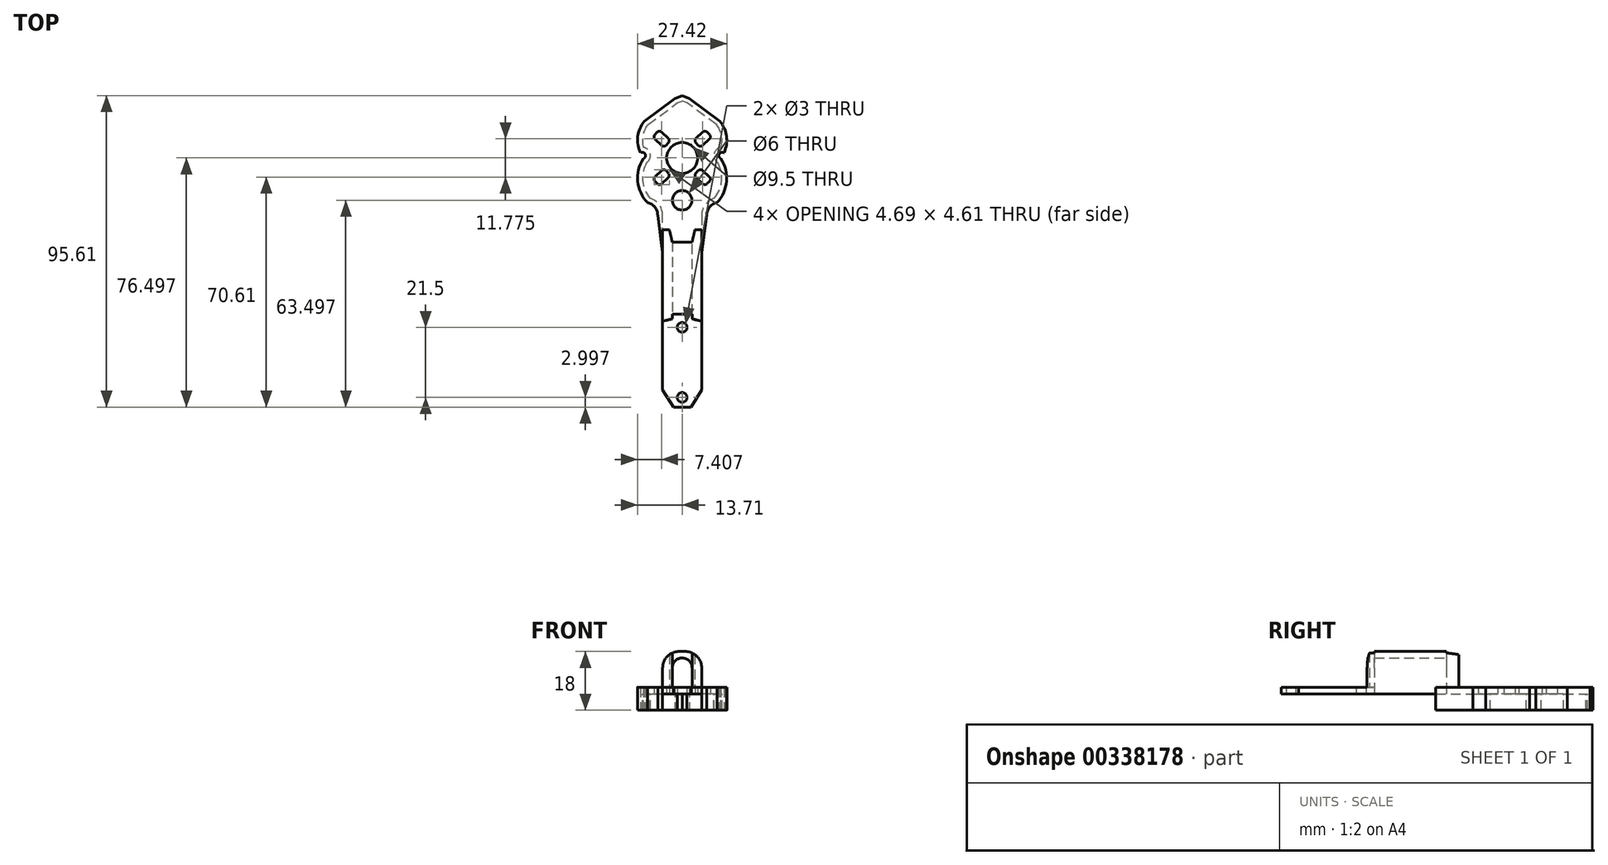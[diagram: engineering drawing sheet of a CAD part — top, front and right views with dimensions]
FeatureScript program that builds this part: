
annotation { "Feature Type Name" : "Feature", "Feature Type Description" : "" }
export const myFeature = defineFeature(function(context is Context, id is Id, definition is map)
    precondition{}
    {
        {
            var Q0;
            Q0=qCreatedBy(makeId("Top.planeOp"),FACE);
            var sketch = newSketch(context, id + "F0", { "sketchPlane" : qUnion([Q0])});
            skLineSegment(sketch, "E0", {"start": v(0, 46.56) * mm, "end": v(0, -47.44) * mm});
            skLineSegment(sketch, "E1", {"start": v(0, 0) * mm, "end": v(6, 0) * mm});
            skLineSegment(sketch, "E2", {"start": v(0, -47.44) * mm, "end": v(0, -44.44) * mm});
            skLineSegment(sketch, "E3", {"start": v(0, -47.44) * mm, "end": v(0, -24.44) * mm});
            skLineSegment(sketch, "E4", {"start": v(0, -47.44) * mm, "end": v(0, 16.06) * mm});
            skLineSegment(sketch, "E5", {"start": v(0, -47.44) * mm, "end": v(0, 29.06) * mm});
            skCircle(sketch, "E6", {"center": v(0, -44.44) * mm, "radius": 1.5 * mm});
            skCircle(sketch, "E7", {"center": v(0, 16.06) * mm, "radius": 3 * mm});
            skCircle(sketch, "E8", {"center": v(0, 29.06) * mm, "radius": 4.75 * mm});
            skLineSegment(sketch, "E9", {"start": v(6, 0) * mm, "end": v(6, -42.14) * mm});
            skLineSegment(sketch, "E10", {"start": v(6, -42.14) * mm, "end": v(2.65, -47.44) * mm});
            skLineSegment(sketch, "E11", {"start": v(2.65, -47.44) * mm, "end": v(0, -47.44) * mm});
            skLineSegment(sketch, "E12.MirrorCS", {"start": v(-6, 0) * mm, "end": v(-6, -42.14) * mm});
            skLineSegment(sketch, "E13.MirrorCS", {"start": v(-6, -42.14) * mm, "end": v(-2.65, -47.44) * mm});
            skLineSegment(sketch, "E14", {"start": v(0, -24.44) * mm, "end": v(0, -22.94) * mm});
            skCircle(sketch, "E15", {"center": v(0, -22.94) * mm, "radius": 1.5 * mm});
            skLineSegment(sketch, "E16.MirrorCS", {"start": v(-2.65, -47.44) * mm, "end": v(0, -47.44) * mm});
            skLineSegment(sketch, "E17.MirrorCS", {"start": v(3.47, 25.82) * mm, "end": v(4.57, 24.8) * mm});
            skLineSegment(sketch, "E18.MirrorCS", {"start": v(-3.47, 25.82) * mm, "end": v(-4.57, 24.8) * mm});
            skLineSegment(sketch, "E19", {"start": v(-8.04, 36.57) * mm, "end": v(-8.38, 36.2) * mm});
            skLineSegment(sketch, "E20", {"start": v(-8.04, 36.57) * mm, "end": v(-7.7, 36.93) * mm});
            skLineSegment(sketch, "E21", {"start": v(-6.28, 36.98) * mm, "end": v(-4.27, 35.1) * mm});
            skLineSegment(sketch, "E22.MirrorCS", {"start": v(-3.47, 32.3) * mm, "end": v(-4.57, 33.32) * mm});
            skLineSegment(sketch, "E23", {"start": v(-4.57, 33.32) * mm, "end": v(-4.23, 33.69) * mm});
            skLineSegment(sketch, "E24.MirrorCS", {"start": v(-4.57, 33.32) * mm, "end": v(-4.9, 32.96) * mm});
            skLineSegment(sketch, "E25.MirrorCS", {"start": v(-8.33, 34.79) * mm, "end": v(-6.32, 32.9) * mm});
            skLineSegment(sketch, "E26.MirrorCS", {"start": v(4.57, 33.32) * mm, "end": v(4.9, 32.96) * mm});
            skLineSegment(sketch, "E27.MirrorCS", {"start": v(4.57, 33.32) * mm, "end": v(4.23, 33.69) * mm});
            skLineSegment(sketch, "E28.MirrorCS", {"start": v(6.28, 36.98) * mm, "end": v(4.27, 35.1) * mm});
            skLineSegment(sketch, "E29.MirrorCS", {"start": v(8.33, 34.79) * mm, "end": v(6.32, 32.9) * mm});
            skLineSegment(sketch, "E30.MirrorCS", {"start": v(8.04, 36.57) * mm, "end": v(8.38, 36.2) * mm});
            skLineSegment(sketch, "E31.MirrorCS", {"start": v(8.04, 36.57) * mm, "end": v(7.7, 36.93) * mm});
            skLineSegment(sketch, "E32.MirrorCS", {"start": v(4.57, 24.8) * mm, "end": v(4.9, 25.16) * mm});
            skLineSegment(sketch, "E33.MirrorCS", {"start": v(4.57, 24.8) * mm, "end": v(4.23, 24.43) * mm});
            skLineSegment(sketch, "E34.MirrorCS", {"start": v(8.04, 21.55) * mm, "end": v(7.7, 21.18) * mm});
            skLineSegment(sketch, "E35.MirrorCS", {"start": v(8.04, 21.55) * mm, "end": v(8.38, 21.91) * mm});
            skLineSegment(sketch, "E36.MirrorCS", {"start": v(-4.57, 24.8) * mm, "end": v(-4.9, 25.16) * mm});
            skLineSegment(sketch, "E37.MirrorCS", {"start": v(-4.57, 24.8) * mm, "end": v(-4.23, 24.43) * mm});
            skLineSegment(sketch, "E38.MirrorCS", {"start": v(-8.04, 21.55) * mm, "end": v(-7.7, 21.18) * mm});
            skLineSegment(sketch, "E39.MirrorCS", {"start": v(-8.04, 21.55) * mm, "end": v(-8.38, 21.91) * mm});
            skLineSegment(sketch, "E40.trimOffspring", {"start": v(6.32, 25.2) * mm, "end": v(8.33, 23.33) * mm});
            skLineSegment(sketch, "E41.trimOffspring", {"start": v(4.27, 23.01) * mm, "end": v(6.28, 21.14) * mm});
            skLineSegment(sketch, "E42.trimOffspring", {"start": v(-6.32, 25.2) * mm, "end": v(-8.33, 23.33) * mm});
            skLineSegment(sketch, "E43.trimOffspring", {"start": v(3.47, 32.3) * mm, "end": v(4.57, 33.32) * mm});
            skPoint(sketch, "E44.end.orphan", {"position": v(4.57, 33.32) * mm});
            skLineSegment(sketch, "E45.trimOffspring", {"start": v(-4.27, 23.01) * mm, "end": v(-6.28, 21.14) * mm});
            skLineSegment(sketch, "E46", {"start": v(-6, 0) * mm, "end": v(-6, 11.41) * mm});
            skLineSegment(sketch, "E47", {"start": v(-6, 11.41) * mm, "end": v(6, 11.41) * mm});
            skLineSegment(sketch, "E48", {"start": v(6, 11.41) * mm, "end": v(6, 0) * mm});
            skArc(sketch, "E49", {"start": v(9.86, 16.68) * mm, "mid": v(7.07, 14.68) * mm, "end": v(6, 11.41) * mm});
            skArc(sketch, "E50", {"start": v(9.86, 16.68) * mm, "mid": v(12.13, 22.04) * mm, "end": v(10.83, 27.72) * mm});
            skArc(sketch, "E51", {"start": v(11.86, 32.27) * mm, "mid": v(12.08, 35.92) * mm, "end": v(10.55, 39.23) * mm});
            skArc(sketch, "E52", {"start": v(11.86, 32.27) * mm, "mid": v(9.81, 30.34) * mm, "end": v(10.83, 27.72) * mm});
            skPoint(sketch, "E52.startSnap0", {"position": v(12.16, 22.87) * mm});
            skPoint(sketch, "E53.orphan", {"position": v(12.16, 32.3) * mm});
            skPoint(sketch, "E54.orphan", {"position": v(9.86, 29.06) * mm});
            skLineSegment(sketch, "E55", {"start": v(10.55, 39.23) * mm, "end": v(1.45, 45.98) * mm});
            skLineSegment(sketch, "E56", {"start": v(1.45, 45.98) * mm, "end": v(0, 46.56) * mm});
            skLineSegment(sketch, "E57.MirrorCS", {"start": v(-10.55, 39.23) * mm, "end": v(-1.45, 45.98) * mm});
            skLineSegment(sketch, "E58.MirrorCS", {"start": v(-1.45, 45.98) * mm, "end": v(0, 46.56) * mm});
            skArc(sketch, "E59.MirrorCS", {"start": v(-11.86, 32.27) * mm, "mid": v(-12.08, 35.92) * mm, "end": v(-10.55, 39.23) * mm});
            skArc(sketch, "E60.MirrorCS", {"start": v(-11.86, 32.27) * mm, "mid": v(-9.81, 30.34) * mm, "end": v(-10.83, 27.72) * mm});
            skArc(sketch, "E61.MirrorCS", {"start": v(-9.86, 16.68) * mm, "mid": v(-12.13, 22.04) * mm, "end": v(-10.83, 27.72) * mm});
            skArc(sketch, "E62.MirrorCS", {"start": v(-9.86, 16.68) * mm, "mid": v(-7.07, 14.68) * mm, "end": v(-6, 11.41) * mm});
            skPoint(sketch, "E63.orphan", {"position": v(-9.86, 39.98) * mm});
            skPoint(sketch, "E64.orphan", {"position": v(9.86, 39.98) * mm});
            skPoint(sketch, "E65.orphan", {"position": v(8.04, 36.57) * mm});
            skPoint(sketch, "E66.orphan", {"position": v(8.04, 21.55) * mm});
            skPoint(sketch, "E67.orphan", {"position": v(-8.04, 21.55) * mm});
            skPoint(sketch, "E68.visualSharp", {"position": v(-7.01, 37.66) * mm});
            skArc(sketch, "E68.filletArc", {"start": v(-6.28, 36.98) * mm, "mid": v(-7, 37.25) * mm, "end": v(-7.7, 36.93) * mm});
            skPoint(sketch, "E69.visualSharp", {"position": v(-9.06, 35.47) * mm});
            skArc(sketch, "E69.filletArc", {"start": v(-8.38, 36.2) * mm, "mid": v(-8.65, 35.48) * mm, "end": v(-8.33, 34.79) * mm});
            skPoint(sketch, "E70.visualSharp", {"position": v(-5.6, 32.23) * mm});
            skArc(sketch, "E70.filletArc", {"start": v(-6.32, 32.9) * mm, "mid": v(-5.6, 32.64) * mm, "end": v(-4.9, 32.96) * mm});
            skPoint(sketch, "E71.visualSharp", {"position": v(-3.54, 34.42) * mm});
            skArc(sketch, "E71.filletArc", {"start": v(-4.23, 33.69) * mm, "mid": v(-3.96, 34.4) * mm, "end": v(-4.27, 35.1) * mm});
            skPoint(sketch, "E72.visualSharp", {"position": v(7.01, 37.66) * mm});
            skArc(sketch, "E72.filletArc", {"start": v(7.7, 36.93) * mm, "mid": v(7, 37.25) * mm, "end": v(6.28, 36.98) * mm});
            skPoint(sketch, "E73.visualSharp", {"position": v(9.06, 35.47) * mm});
            skArc(sketch, "E73.filletArc", {"start": v(8.33, 34.79) * mm, "mid": v(8.65, 35.48) * mm, "end": v(8.38, 36.2) * mm});
            skPoint(sketch, "E74.visualSharp", {"position": v(5.6, 32.23) * mm});
            skArc(sketch, "E74.filletArc", {"start": v(4.9, 32.96) * mm, "mid": v(5.6, 32.64) * mm, "end": v(6.32, 32.9) * mm});
            skPoint(sketch, "E75.visualSharp", {"position": v(3.54, 34.42) * mm});
            skArc(sketch, "E75.filletArc", {"start": v(4.27, 35.1) * mm, "mid": v(3.96, 34.4) * mm, "end": v(4.23, 33.69) * mm});
            skPoint(sketch, "E76.visualSharp", {"position": v(-5.6, 25.89) * mm});
            skArc(sketch, "E76.filletArc", {"start": v(-4.9, 25.16) * mm, "mid": v(-5.6, 25.47) * mm, "end": v(-6.32, 25.2) * mm});
            skPoint(sketch, "E77.visualSharp", {"position": v(-3.54, 23.7) * mm});
            skArc(sketch, "E77.filletArc", {"start": v(-4.27, 23.01) * mm, "mid": v(-3.96, 23.7) * mm, "end": v(-4.23, 24.43) * mm});
            skPoint(sketch, "E78.visualSharp", {"position": v(-7.01, 20.45) * mm});
            skArc(sketch, "E78.filletArc", {"start": v(-7.7, 21.18) * mm, "mid": v(-7, 20.87) * mm, "end": v(-6.28, 21.14) * mm});
            skPoint(sketch, "E79.visualSharp", {"position": v(-9.06, 22.64) * mm});
            skArc(sketch, "E79.filletArc", {"start": v(-8.33, 23.33) * mm, "mid": v(-8.65, 22.63) * mm, "end": v(-8.38, 21.91) * mm});
            skPoint(sketch, "E80.visualSharp", {"position": v(7.01, 20.45) * mm});
            skArc(sketch, "E80.filletArc", {"start": v(6.28, 21.14) * mm, "mid": v(7, 20.87) * mm, "end": v(7.7, 21.18) * mm});
            skPoint(sketch, "E81.visualSharp", {"position": v(9.06, 22.64) * mm});
            skArc(sketch, "E81.filletArc", {"start": v(8.38, 21.91) * mm, "mid": v(8.65, 22.63) * mm, "end": v(8.33, 23.33) * mm});
            skPoint(sketch, "E82.visualSharp", {"position": v(5.6, 25.89) * mm});
            skArc(sketch, "E82.filletArc", {"start": v(6.32, 25.2) * mm, "mid": v(5.6, 25.47) * mm, "end": v(4.9, 25.16) * mm});
            skPoint(sketch, "E83.visualSharp", {"position": v(3.54, 23.7) * mm});
            skArc(sketch, "E83.filletArc", {"start": v(4.23, 24.43) * mm, "mid": v(3.96, 23.7) * mm, "end": v(4.27, 23.01) * mm});
            skArc(sketch, "E84.0", {"start": v(10.67, 15.35) * mm, "mid": v(8.4, 13.94) * mm, "end": v(7.5, 11.41) * mm});
            skArc(sketch, "E84.1", {"start": v(10.67, 15.35) * mm, "mid": v(13.62, 21.88) * mm, "end": v(11.9, 28.84) * mm});
            skArc(sketch, "E84.2", {"start": v(-12.83, 30.63) * mm, "mid": v(-13.64, 35.66) * mm, "end": v(-11.59, 40.33) * mm});
            skArc(sketch, "E84.3", {"start": v(-12.83, 30.63) * mm, "mid": v(-11.36, 30.25) * mm, "end": v(-11.9, 28.84) * mm});
            skArc(sketch, "E84.4", {"start": v(-10.67, 15.35) * mm, "mid": v(-13.62, 21.88) * mm, "end": v(-11.9, 28.84) * mm});
            skArc(sketch, "E84.5", {"start": v(-10.67, 15.35) * mm, "mid": v(-8.4, 13.94) * mm, "end": v(-7.5, 11.41) * mm});
            skLineSegment(sketch, "E84.6", {"start": v(-11.59, 40.33) * mm, "end": v(-2.18, 47.3) * mm});
            skLineSegment(sketch, "E84.7", {"start": v(-2.18, 47.3) * mm, "end": v(0, 48.17) * mm});
            skLineSegment(sketch, "E84.8", {"start": v(2.18, 47.3) * mm, "end": v(0, 48.17) * mm});
            skLineSegment(sketch, "E84.9", {"start": v(11.59, 40.33) * mm, "end": v(2.18, 47.3) * mm});
            skArc(sketch, "E84.10", {"start": v(12.83, 30.63) * mm, "mid": v(13.64, 35.66) * mm, "end": v(11.59, 40.33) * mm});
            skArc(sketch, "E84.11", {"start": v(12.83, 30.63) * mm, "mid": v(11.36, 30.25) * mm, "end": v(11.9, 28.84) * mm});
            skLineSegment(sketch, "E85", {"start": v(-7.5, 11.41) * mm, "end": v(-6, 0) * mm});
            skLineSegment(sketch, "E86", {"start": v(7.5, 11.41) * mm, "end": v(6, 0) * mm});
            skLineSegment(sketch, "E87", {"start": v(0, -21.44) * mm, "end": v(0, 3.23) * mm});
            skLineSegment(sketch, "E88", {"start": v(0, 3.23) * mm, "end": v(3.04, 3.23) * mm});
            skLineSegment(sketch, "E89.MirrorCS", {"start": v(0, 3.23) * mm, "end": v(-3.04, 3.23) * mm});
            skLineSegment(sketch, "E90", {"start": v(-3.04, 3.23) * mm, "end": v(-3.04, -18.85) * mm});
            skLineSegment(sketch, "E91", {"start": v(-3.04, -18.85) * mm, "end": v(3.04, -18.85) * mm});
            skLineSegment(sketch, "E92", {"start": v(3.04, -18.85) * mm, "end": v(3.04, 3.23) * mm});
            skLineSegment(sketch, "E93", {"start": v(0, 7) * mm, "end": v(-6, 7) * mm});
            skLineSegment(sketch, "E94.MirrorCS", {"start": v(0, 7) * mm, "end": v(6, 7) * mm});
            skLineSegment(sketch, "E95", {"start": v(-6, -21.07) * mm, "end": v(0, -19.59) * mm});
            skLineSegment(sketch, "E96.MirrorCS", {"start": v(6, -21.07) * mm, "end": v(0, -19.59) * mm});
            skLineSegment(sketch, "E97", {"start": v(-3, -20.33) * mm, "end": v(-3.04, -18.85) * mm});
            skLineSegment(sketch, "E98", {"start": v(3.04, -18.85) * mm, "end": v(3.04, -20.34) * mm});
            skLineSegment(sketch, "E99", {"start": v(-3.04, 3.23) * mm, "end": v(-3.9, 7) * mm});
            skLineSegment(sketch, "E100.MirrorCS", {"start": v(3.04, 3.23) * mm, "end": v(3.9, 7) * mm});
            skSolve(sketch);
        }
        {
            var Q0;
            {var subQ0=sQuery(id+"F0.wireOp",EDGE,"E13.MirrorCS");Q0=makeQuery(id+"F0.imprint","IMPRINT",FACE,{"disambiguationData":[TD([[makeQuery(id+"F0.imprint","IMPRINT",EDGE,{"derivedFrom":subQ0}),1.0]])]});}
            var Q1;
            {var subQ0=sQuery(id+"F0.wireOp",EDGE,"E10");Q1=makeQuery(id+"F0.imprint","IMPRINT",FACE,{"disambiguationData":[TD([[makeQuery(id+"F0.imprint","IMPRINT",EDGE,{"derivedFrom":subQ0}),-1.0]])]});}
            var Q2;
            {var subQ1=sQuery(id+"F0.wireOp",EDGE,"E49");Q2=makeQuery(id+"F0.imprint","IMPRINT",FACE,{"disambiguationData":[TD([[makeQuery(id+"F0.imprint","IMPRINT",EDGE,{"derivedFrom":subQ1}),1.0]])]});}
            var Q3;
            Q3=makeQuery(id+"F0.imprint","IMPRINT",FACE,{"disambiguationData":[TD([[makeQuery(id+"F0.imprint","IMPRINT",EDGE,{"derivedFrom":sQuery(id+"F0.wireOp",EDGE,"E19")}),-1.0]])]});
            var Q4;
            Q4=makeQuery(id+"F0.imprint","IMPRINT",FACE,{"disambiguationData":[TD([[makeQuery(id+"F0.imprint","IMPRINT",EDGE,{"derivedFrom":sQuery(id+"F0.wireOp",EDGE,"E26.MirrorCS")}),-1.0]])]});
            var Q5;
            {var subQ0=sQuery(id+"F0.wireOp",EDGE,"E94.MirrorCS");Q5=makeQuery(id+"F0.imprint","IMPRINT",FACE,{"disambiguationData":[TD([[makeQuery(id+"F0.imprint","IMPRINT",EDGE,{"derivedFrom":subQ0}),1.0]])]});}
            var Q6;
            {var subQ0=sQuery(id+"F0.wireOp",EDGE,"E93");Q6=makeQuery(id+"F0.imprint","IMPRINT",FACE,{"disambiguationData":[TD([[makeQuery(id+"F0.imprint","IMPRINT",EDGE,{"derivedFrom":subQ0}),-1.0]])]});}
            var Q7;
            {var subQ5=sQuery(id+"F0.wireOp",EDGE,"E98");Q7=makeQuery(id+"F0.imprint","IMPRINT",FACE,{"disambiguationData":[TD([[makeQuery(id+"F0.imprint","IMPRINT",EDGE,{"derivedFrom":subQ5}),-1.0]])]});}
            var Q8;
            {var subQ5=sQuery(id+"F0.wireOp",EDGE,"E97");Q8=makeQuery(id+"F0.imprint","IMPRINT",FACE,{"disambiguationData":[TD([[makeQuery(id+"F0.imprint","IMPRINT",EDGE,{"derivedFrom":subQ5}),-1.0]])]});}
            var Q9;
            {var subQ0=sQuery(id+"F0.wireOp",EDGE,"E89.MirrorCS");Q9=makeQuery(id+"F0.imprint","IMPRINT",FACE,{"disambiguationData":[TD([[makeQuery(id+"F0.imprint","IMPRINT",EDGE,{"derivedFrom":subQ0}),-1.0]])]});}
            var Q10;
            {var subQ0=sQuery(id+"F0.wireOp",EDGE,"E88");Q10=makeQuery(id+"F0.imprint","IMPRINT",FACE,{"disambiguationData":[TD([[makeQuery(id+"F0.imprint","IMPRINT",EDGE,{"derivedFrom":subQ0}),1.0]])]});}
            extrude(context, id + "F1", {"entities" : qUnion([Q0, Q1, Q2, Q3, Q4, Q5, Q6, Q7, Q8, Q9, Q10]), "depth" : 2 * mm});
        }
        {
            var Q0;
            {var subQ5=sQuery(id+"F0.wireOp",EDGE,"E88");Q0=makeQuery(id+"F0.imprint","IMPRINT",FACE,{"disambiguationData":[TD([[makeQuery(id+"F0.imprint","IMPRINT",EDGE,{"derivedFrom":subQ5}),-1.0]])]});}
            var Q1;
            Q1=makeQuery(id+"F0.imprint","IMPRINT",FACE,{"disambiguationData":[TD([[makeQuery(id+"F0.imprint","IMPRINT",EDGE,{"derivedFrom":sQuery(id+"F0.wireOp",EDGE,"E90")}),-1.0]])]});
            var Q2;
            {var subQ0=sQuery(id+"F0.wireOp",EDGE,"E87");var subQ1=sQuery(id+"F0.wireOp",EDGE,"E1");var subQ2=makeQuery(id+"F0.imprint","INTERSECT",VERTEX,{"derivedFrom":[subQ1,subQ0]});Q2=makeQuery(id+"F0.imprint","IMPRINT",FACE,{"disambiguationData":[TD([[makeQuery(id+"F0.imprint","IMPRINT",EDGE,{"disambiguationData":[TD([[subQ2,-1.0]])],"derivedFrom":subQ1}),-1.0]])]});}
            var Q3;
            {var subQ1=sQuery(id+"F0.wireOp",EDGE,"E89.MirrorCS");Q3=makeQuery(id+"F0.imprint","IMPRINT",FACE,{"disambiguationData":[TD([[makeQuery(id+"F0.imprint","IMPRINT",EDGE,{"derivedFrom":subQ1}),1.0]])]});}
            var Q4;
            {var subQ3=sQuery(id+"F0.wireOp",EDGE,"E98");Q4=makeQuery(id+"F0.imprint","IMPRINT",FACE,{"disambiguationData":[TD([[makeQuery(id+"F0.imprint","IMPRINT",EDGE,{"derivedFrom":subQ3}),1.0]])]});}
            var Q5;
            {var subQ0=sQuery(id+"F0.wireOp",EDGE,"E100.MirrorCS");Q5=makeQuery(id+"F0.imprint","IMPRINT",FACE,{"disambiguationData":[TD([[makeQuery(id+"F0.imprint","IMPRINT",EDGE,{"derivedFrom":subQ0}),-1.0]])]});}
            extrude(context, id + "F2", {"entities" : qUnion([Q0, Q1, Q2, Q3, Q4, Q5]), "operationType" : NewBodyOperationType.ADD, "depth" : 13 * mm});
        }
        {
            var Q0;
            {var subQ1=sQuery(id+"F0.wireOp",EDGE,"E89.MirrorCS");Q0=makeQuery(id+"F0.imprint","IMPRINT",FACE,{"disambiguationData":[TD([[makeQuery(id+"F0.imprint","IMPRINT",EDGE,{"derivedFrom":subQ1}),1.0]])]});}
            var Q1;
            {var subQ0=sQuery(id+"F0.wireOp",EDGE,"E87");var subQ1=sQuery(id+"F0.wireOp",EDGE,"E1");var subQ2=makeQuery(id+"F0.imprint","INTERSECT",VERTEX,{"derivedFrom":[subQ1,subQ0]});Q1=makeQuery(id+"F0.imprint","IMPRINT",FACE,{"disambiguationData":[TD([[makeQuery(id+"F0.imprint","IMPRINT",EDGE,{"disambiguationData":[TD([[subQ2,-1.0]])],"derivedFrom":subQ1}),-1.0]])]});}
            var Q2;
            {var subQ5=sQuery(id+"F0.wireOp",EDGE,"E88");Q2=makeQuery(id+"F0.imprint","IMPRINT",FACE,{"disambiguationData":[TD([[makeQuery(id+"F0.imprint","IMPRINT",EDGE,{"derivedFrom":subQ5}),-1.0]])]});}
            extrude(context, id + "F3", {"entities" : qUnion([Q0, Q1, Q2]), "operationType" : NewBodyOperationType.REMOVE, "depth" : 11 * mm});
        }
        {
            var Q0;
            Q0=makeQuery(id+"F3.boolean.opBoolean","COPY",EDGE,{"derivedFrom":makeQuery(id+"F3.opExtrude","CAP_EDGE",EDGE,{"disambiguationData":[OSD([sQuery(id+"F0.wireOp",EDGE,"E90")])],"isStart":false})});
            var Q1;
            Q1=makeQuery(id+"F3.boolean.opBoolean","COPY",EDGE,{"derivedFrom":makeQuery(id+"F3.opExtrude","CAP_EDGE",EDGE,{"disambiguationData":[OSD([sQuery(id+"F0.wireOp",EDGE,"E92")])],"isStart":false})});
            fillet(context, id + "F4", {"entities" : qUnion([Q0, Q1]), "radius" : 3 * mm, "tangentPropagation" : true, "allowEdgeOverflow" : false});
        }
        {
            var Q0;
            {var subQ1=sQuery(id+"F0.wireOp",EDGE,"E49");Q0=makeQuery(id+"F0.imprint","IMPRINT",FACE,{"disambiguationData":[TD([[makeQuery(id+"F0.imprint","IMPRINT",EDGE,{"derivedFrom":subQ1}),1.0]])]});}
            extrude(context, id + "F5", {"entities" : qUnion([Q0]), "operationType" : NewBodyOperationType.ADD, "oppositeDirection" : true, "depth" : 5 * mm});
        }
        {
            var Q0;
            Q0=makeQuery(id+"F2.opExtrude","CAP_EDGE",EDGE,{"disambiguationData":[OSD([sQuery(id+"F0.wireOp",EDGE,"E9"),sQuery(id+"F0.wireOp",EDGE,"E48")])],"isStart":false});
            var Q1;
            Q1=makeQuery(id+"F2.opExtrude","CAP_EDGE",EDGE,{"disambiguationData":[OSD([sQuery(id+"F0.wireOp",EDGE,"E12.MirrorCS"),sQuery(id+"F0.wireOp",EDGE,"E46")])],"isStart":false});
            fillet(context, id + "F6", {"entities" : qUnion([Q0, Q1]), "radius" : 5 * mm, "tangentPropagation" : true, "allowEdgeOverflow" : false});
        }
    });
